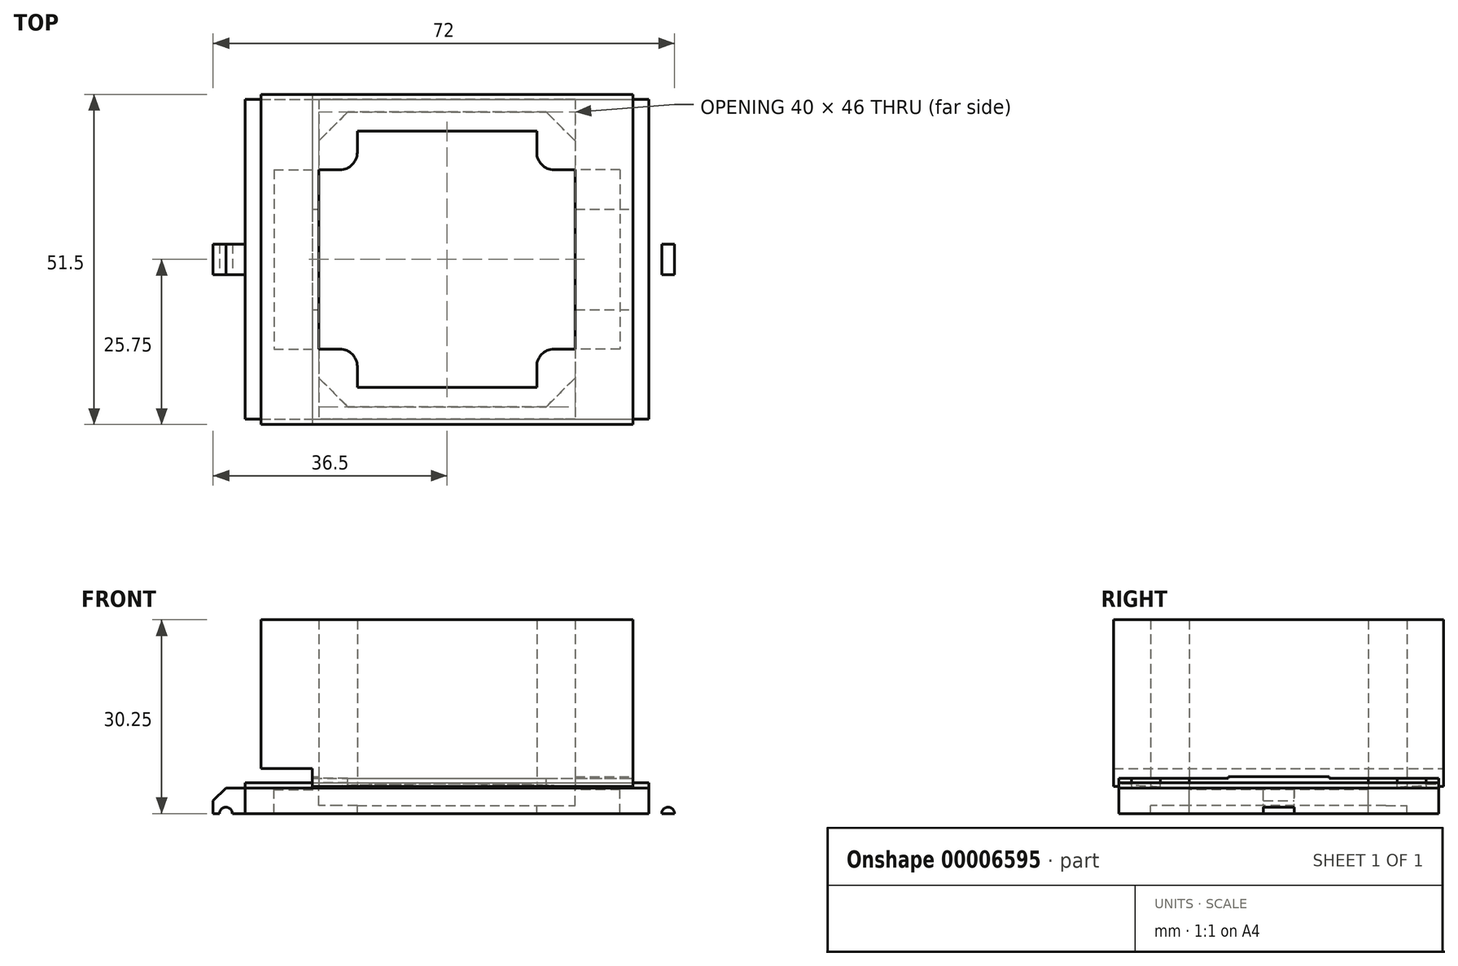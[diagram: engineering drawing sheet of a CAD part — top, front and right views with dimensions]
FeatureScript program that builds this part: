
annotation { "Feature Type Name" : "Feature", "Feature Type Description" : "" }
export const myFeature = defineFeature(function(context is Context, id is Id, definition is map)
    precondition{}
    {
        {
            var Q0;
            Q0=qCreatedBy(makeId("Top.planeOp"),FACE);
            var sketch = newSketch(context, id + "F0", { "sketchPlane" : qUnion([Q0])});
            skLineSegment(sketch, "E0.bottom", {"start": v(0, 0) * mm, "end": v(-58, 0) * mm});
            skLineSegment(sketch, "E0.top", {"start": v(0, 51.5) * mm, "end": v(-58, 51.5) * mm});
            skLineSegment(sketch, "E0.left", {"start": v(0, 0) * mm, "end": v(0, 51.5) * mm});
            skLineSegment(sketch, "E0.right", {"start": v(-58, 0) * mm, "end": v(-58, 51.5) * mm});
            skLineSegment(sketch, "E1", {"start": v(-50, 51.5) * mm, "end": v(-50, 0) * mm});
            skLineSegment(sketch, "E2", {"start": v(-50, 50.7) * mm, "end": v(0, 50.7) * mm});
            skLineSegment(sketch, "E3", {"start": v(-50, 33.6) * mm, "end": v(0, 33.6) * mm});
            skPoint(sketch, "E4", {"position": v(0, 25.75) * mm});
            skLineSegment(sketch, "E5", {"start": v(0, 25.75) * mm, "end": v(-50, 25.75) * mm, "construction": true});
            skLineSegment(sketch, "E6.0.MirrorCS", {"start": v(-50, 0.8) * mm, "end": v(0, 0.8) * mm});
            skLineSegment(sketch, "E6.1.MirrorCS", {"start": v(-50, 17.9) * mm, "end": v(0, 17.9) * mm});
            skSolve(sketch);
        }
        {
            var Q0;
            {var subQ9=sQuery(id+"F0.wireOp",EDGE,"E0.right");Q0=makeQuery(id+"F0.imprint","IMPRINT",FACE,{"disambiguationData":[TD([[makeQuery(id+"F0.imprint","IMPRINT",EDGE,{"derivedFrom":subQ9}),-1.0]])]});}
            var Q1;
            {var subQ1=sQuery(id+"F0.wireOp",EDGE,"E2");Q1=makeQuery(id+"F0.imprint","IMPRINT",FACE,{"disambiguationData":[TD([[makeQuery(id+"F0.imprint","IMPRINT",EDGE,{"derivedFrom":subQ1}),1.0]])]});}
            var Q2;
            {var subQ1=sQuery(id+"F0.wireOp",EDGE,"E2");Q2=makeQuery(id+"F0.imprint","IMPRINT",FACE,{"disambiguationData":[TD([[makeQuery(id+"F0.imprint","IMPRINT",EDGE,{"derivedFrom":subQ1}),-1.0]])]});}
            var Q3;
            {var subQ1=sQuery(id+"F0.wireOp",EDGE,"E3");Q3=makeQuery(id+"F0.imprint","IMPRINT",FACE,{"disambiguationData":[TD([[makeQuery(id+"F0.imprint","IMPRINT",EDGE,{"derivedFrom":subQ1}),-1.0]])]});}
            var Q4;
            {var subQ1=sQuery(id+"F0.wireOp",EDGE,"E6.0.MirrorCS");Q4=makeQuery(id+"F0.imprint","IMPRINT",FACE,{"disambiguationData":[TD([[makeQuery(id+"F0.imprint","IMPRINT",EDGE,{"derivedFrom":subQ1}),1.0]])]});}
            var Q5;
            {var subQ0=sQuery(id+"F0.wireOp",EDGE,"E6.0.MirrorCS");Q5=makeQuery(id+"F0.imprint","IMPRINT",FACE,{"disambiguationData":[TD([[makeQuery(id+"F0.imprint","IMPRINT",EDGE,{"derivedFrom":subQ0}),-1.0]])]});}
            extrude(context, id + "F1", {"entities" : qUnion([Q0, Q1, Q2, Q3, Q4, Q5]), "depth" : 26 * mm});
        }
        {
            var Q0;
            {var subQ1=sQuery(id+"F0.wireOp",EDGE,"E6.0.MirrorCS");Q0=makeQuery(id+"F0.imprint","IMPRINT",FACE,{"disambiguationData":[TD([[makeQuery(id+"F0.imprint","IMPRINT",EDGE,{"derivedFrom":subQ1}),1.0]])]});}
            var Q1;
            {var subQ1=sQuery(id+"F0.wireOp",EDGE,"E2");Q1=makeQuery(id+"F0.imprint","IMPRINT",FACE,{"disambiguationData":[TD([[makeQuery(id+"F0.imprint","IMPRINT",EDGE,{"derivedFrom":subQ1}),-1.0]])]});}
            extrude(context, id + "F2", {"entities" : qUnion([Q0, Q1]), "operationType" : NewBodyOperationType.REMOVE, "depth" : 1.25 * mm});
        }
        {
            var Q0;
            {var subQ1=sQuery(id+"F0.wireOp",EDGE,"E3");Q0=makeQuery(id+"F0.imprint","IMPRINT",FACE,{"disambiguationData":[TD([[makeQuery(id+"F0.imprint","IMPRINT",EDGE,{"derivedFrom":subQ1}),-1.0]])]});}
            extrude(context, id + "F3", {"entities" : qUnion([Q0]), "operationType" : NewBodyOperationType.REMOVE, "depth" : 1.5 * mm});
        }
        {
            var Q0;
            {var subQ9=sQuery(id+"F0.wireOp",EDGE,"E0.right");Q0=makeQuery(id+"F0.imprint","IMPRINT",FACE,{"disambiguationData":[TD([[makeQuery(id+"F0.imprint","IMPRINT",EDGE,{"derivedFrom":subQ9}),-1.0]])]});}
            extrude(context, id + "F4", {"entities" : qUnion([Q0]), "operationType" : NewBodyOperationType.REMOVE, "depth" : 2.75 * mm});
        }
        {
            var Q0;
            Q0=makeQuery(id+"F2.boolean.opBoolean","COPY",FACE,{"derivedFrom":makeQuery(id+"F2.opExtrude","CAP_FACE",FACE,{"disambiguationData":[OSD([sQuery(id+"F0.wireOp",EDGE,"E0.left"),sQuery(id+"F0.wireOp",EDGE,"E1"),sQuery(id+"F0.wireOp",EDGE,"E6.0.MirrorCS"),sQuery(id+"F0.wireOp",EDGE,"E6.1.MirrorCS")])],"isStart":false})});
            var sketch = newSketch(context, id + "F5", { "sketchPlane" : qUnion([Q0])});
            skLineSegment(sketch, "E7.bottom", {"start": v(-49, -45.75) * mm, "end": v(-9, -45.75) * mm});
            skLineSegment(sketch, "E7.top", {"start": v(-49, -5.75) * mm, "end": v(-9, -5.75) * mm});
            skLineSegment(sketch, "E7.left", {"start": v(-49, -45.75) * mm, "end": v(-49, -5.75) * mm});
            skLineSegment(sketch, "E7.right", {"start": v(-9, -45.75) * mm, "end": v(-9, -5.75) * mm});
            skLineSegment(sketch, "E8.bottom", {"start": v(-49, -48.75) * mm, "end": v(-9, -48.75) * mm});
            skLineSegment(sketch, "E8.top", {"start": v(-49, -2.75) * mm, "end": v(-9, -2.75) * mm});
            skLineSegment(sketch, "E8.left", {"start": v(-49, -48.75) * mm, "end": v(-49, -45.75) * mm});
            skLineSegment(sketch, "E8.right", {"start": v(-9, -48.75) * mm, "end": v(-9, -2.75) * mm});
            skLineSegment(sketch, "E9", {"start": v(-49, -5.75) * mm, "end": v(-49, -2.75) * mm});
            skLineSegment(sketch, "E10", {"start": v(-44.5, -48.75) * mm, "end": v(-49, -44.25) * mm});
            skPoint(sketch, "E11", {"position": v(-43, -5.75) * mm});
            skArc(sketch, "E12", {"start": v(-44.5, -48.75) * mm, "mid": v(-45.82, -45.57) * mm, "end": v(-49, -44.25) * mm, "construction": true});
            skArc(sketch, "E13", {"start": v(-49, -11.75) * mm, "mid": v(-44.76, -10) * mm, "end": v(-43, -5.75) * mm, "construction": true});
            skPoint(sketch, "E14", {"position": v(-49, -11.75) * mm});
            skLineSegment(sketch, "E15", {"start": v(-49, -11.75) * mm, "end": v(-45.7, -11.75) * mm});
            skLineSegment(sketch, "E16", {"start": v(-43, -9.05) * mm, "end": v(-43, -5.75) * mm});
            skPoint(sketch, "E17.visualSharp", {"position": v(-43, -11.75) * mm});
            skArc(sketch, "E17.filletArc", {"start": v(-45.7, -11.75) * mm, "mid": v(-43.8, -10.96) * mm, "end": v(-43, -9.05) * mm});
            skLineSegment(sketch, "E18.1.0", {"start": v(-43, -45.75) * mm, "end": v(-43, -42.45) * mm});
            skArc(sketch, "E18.1.1", {"start": v(-43, -42.45) * mm, "mid": v(-43.8, -40.54) * mm, "end": v(-45.7, -39.75) * mm});
            skLineSegment(sketch, "E18.1.2", {"start": v(-45.7, -39.75) * mm, "end": v(-49, -39.75) * mm});
            skLineSegment(sketch, "E18.2.0", {"start": v(-2, -39.75) * mm, "end": v(-12.3, -39.75) * mm});
            skArc(sketch, "E18.2.1", {"start": v(-12.3, -39.75) * mm, "mid": v(-14.2, -40.54) * mm, "end": v(-15, -42.45) * mm});
            skLineSegment(sketch, "E18.2.2", {"start": v(-15, -42.45) * mm, "end": v(-15, -45.75) * mm});
            skLineSegment(sketch, "E18.3.0", {"start": v(-15, -5.75) * mm, "end": v(-15, -9.05) * mm});
            skArc(sketch, "E18.3.1", {"start": v(-15, -9.05) * mm, "mid": v(-14.2, -10.96) * mm, "end": v(-12.3, -11.75) * mm});
            skLineSegment(sketch, "E18.3.2", {"start": v(-12.3, -11.75) * mm, "end": v(-9, -11.75) * mm});
            skPoint(sketch, "E18.center", {"position": v(-29, -25.75) * mm});
            skLineSegment(sketch, "E19", {"start": v(-29, -25.75) * mm, "end": v(-49, -25.75) * mm, "construction": true});
            skLineSegment(sketch, "E20", {"start": v(-29, -25.75) * mm, "end": v(-29, -45.75) * mm, "construction": true});
            skLineSegment(sketch, "E21.0.MirrorCS", {"start": v(-44.5, -2.75) * mm, "end": v(-49, -7.25) * mm});
            skLineSegment(sketch, "E22.0.MirrorCS", {"start": v(-13.5, -48.75) * mm, "end": v(-9, -44.25) * mm});
            skLineSegment(sketch, "E23.0.MirrorCS", {"start": v(-13.5, -2.75) * mm, "end": v(-9, -7.25) * mm});
            skLineSegment(sketch, "E24.0", {"start": v(0, -25.75) * mm, "end": v(-50, -25.75) * mm, "construction": true});
            skLineSegment(sketch, "E25.0", {"start": v(0, 0) * mm, "end": v(-58, 0) * mm});
            skPoint(sketch, "E26", {"position": v(-29, 0) * mm});
            skPoint(sketch, "E27.orphan", {"position": v(-9, -39.75) * mm});
            skLineSegment(sketch, "E28", {"start": v(-2, -39.75) * mm, "end": v(-2, -11.75) * mm});
            skLineSegment(sketch, "E29", {"start": v(-2, -11.75) * mm, "end": v(-9, -11.75) * mm});
            skPoint(sketch, "E30", {"position": v(-6, -39.75) * mm});
            skLineSegment(sketch, "E31", {"start": v(-6, -39.75) * mm, "end": v(-6, -11.75) * mm});
            skLineSegment(sketch, "E32.0.MirrorCS", {"start": v(-56, -39.75) * mm, "end": v(-45.7, -39.75) * mm});
            skLineSegment(sketch, "E32.1.MirrorCS", {"start": v(-56, -39.75) * mm, "end": v(-56, -11.75) * mm});
            skLineSegment(sketch, "E32.2.MirrorCS", {"start": v(-56, -11.75) * mm, "end": v(-49, -11.75) * mm});
            skLineSegment(sketch, "E32.3.MirrorCS", {"start": v(-52, -39.75) * mm, "end": v(-52, -11.75) * mm});
            skSolve(sketch);
        }
        {
            var Q0;
            {var subQ1=sQuery(id+"F5.wireOp",EDGE,"E7.bottom");var subQ9=makeQuery(id+"F5.imprint","INTERSECT",VERTEX,{"derivedFrom":[subQ1,sQuery(id+"F5.wireOp",EDGE,"E18.1.0")]});Q0=makeQuery(id+"F5.imprint","IMPRINT",FACE,{"disambiguationData":[TD([[makeQuery(id+"F5.imprint","IMPRINT",EDGE,{"disambiguationData":[TD([[subQ9,1.0]])],"derivedFrom":subQ1}),-1.0]])]});}
            var Q1;
            {var subQ0=sQuery(id+"F5.wireOp",EDGE,"E18.1.0");Q1=makeQuery(id+"F5.imprint","IMPRINT",FACE,{"disambiguationData":[TD([[makeQuery(id+"F5.imprint","IMPRINT",EDGE,{"derivedFrom":subQ0}),1.0]])]});}
            var Q2;
            {var subQ6=sQuery(id+"F5.wireOp",EDGE,"E18.2.1");Q2=makeQuery(id+"F5.imprint","IMPRINT",FACE,{"disambiguationData":[TD([[makeQuery(id+"F5.imprint","IMPRINT",EDGE,{"derivedFrom":subQ6}),1.0]])]});}
            var Q3;
            {var subQ10=sQuery(id+"F5.wireOp",EDGE,"E18.1.0");Q3=makeQuery(id+"F5.imprint","IMPRINT",FACE,{"disambiguationData":[TD([[makeQuery(id+"F5.imprint","IMPRINT",EDGE,{"derivedFrom":subQ10}),-1.0]])]});}
            var Q4;
            {var subQ7=sQuery(id+"F5.wireOp",EDGE,"E15");Q4=makeQuery(id+"F5.imprint","IMPRINT",FACE,{"disambiguationData":[TD([[makeQuery(id+"F5.imprint","IMPRINT",EDGE,{"derivedFrom":subQ7}),-1.0]])]});}
            var Q5;
            {var subQ6=sQuery(id+"F5.wireOp",EDGE,"E15");Q5=makeQuery(id+"F5.imprint","IMPRINT",FACE,{"disambiguationData":[TD([[makeQuery(id+"F5.imprint","IMPRINT",EDGE,{"derivedFrom":subQ6}),1.0]])]});}
            var Q6;
            {var subQ6=sQuery(id+"F5.wireOp",EDGE,"E18.3.0");Q6=makeQuery(id+"F5.imprint","IMPRINT",FACE,{"disambiguationData":[TD([[makeQuery(id+"F5.imprint","IMPRINT",EDGE,{"derivedFrom":subQ6}),1.0]])]});}
            var Q7;
            {var subQ1=sQuery(id+"F5.wireOp",EDGE,"E7.top");var subQ8=makeQuery(id+"F5.imprint","INTERSECT",VERTEX,{"derivedFrom":[subQ1,sQuery(id+"F5.wireOp",EDGE,"E16")]});Q7=makeQuery(id+"F5.imprint","IMPRINT",FACE,{"disambiguationData":[TD([[makeQuery(id+"F5.imprint","IMPRINT",EDGE,{"disambiguationData":[TD([[subQ8,1.0]])],"derivedFrom":subQ1}),1.0]])]});}
            extrude(context, id + "F6", {"entities" : qUnion([Q0, Q1, Q2, Q3, Q4, Q5, Q6, Q7]), "depth" : 1.5 * mm});
        }
        {
            var Q0;
            {var subQ10=sQuery(id+"F5.wireOp",EDGE,"E18.1.0");Q0=makeQuery(id+"F5.imprint","IMPRINT",FACE,{"disambiguationData":[TD([[makeQuery(id+"F5.imprint","IMPRINT",EDGE,{"derivedFrom":subQ10}),-1.0]])]});}
            var Q1;
            {var subQ7=sQuery(id+"F5.wireOp",EDGE,"E15");Q1=makeQuery(id+"F5.imprint","IMPRINT",FACE,{"disambiguationData":[TD([[makeQuery(id+"F5.imprint","IMPRINT",EDGE,{"derivedFrom":subQ7}),-1.0]])]});}
            extrude(context, id + "F7", {"entities" : qUnion([Q0, Q1]), "operationType" : NewBodyOperationType.ADD, "depth" : 4.25 * mm});
        }
        {
            var Q0;
            {var subQ0=sQuery(id+"F5.wireOp",EDGE,"E8.top");var subQ1=sQuery(id+"F5.wireOp",EDGE,"E8.right");var subQ2=sQuery(id+"F5.wireOp",EDGE,"E7.left");var subQ3=sQuery(id+"F5.wireOp",EDGE,"E21.0.MirrorCS");var subQ4=sQuery(id+"F5.wireOp",EDGE,"E23.0.MirrorCS");Q0=makeQuery(id+"F7.boolean.opBoolean","SPLIT",FACE,{"disambiguationData":[TD([makeQuery(id+"F6.opExtrude","SWEPT_FACE",FACE,{"disambiguationData":[OSD([subQ0])]})])],"derivedFrom":makeQuery(id+"F6.opExtrude","CAP_FACE",FACE,{"disambiguationData":[OSD([sQuery(id+"F5.wireOp",EDGE,"E8.bottom"),subQ0,subQ1,subQ2,sQuery(id+"F5.wireOp",EDGE,"E10"),subQ3,sQuery(id+"F5.wireOp",EDGE,"E22.0.MirrorCS"),subQ4])],"isStart":false})});}
            var sketch = newSketch(context, id + "F8", { "sketchPlane" : qUnion([Q0])});
            skLineSegment(sketch, "E33.0", {"start": v(-2, -11.75) * mm, "end": v(-9, -11.75) * mm});
            skLineSegment(sketch, "E34.0", {"start": v(-6, -39.75) * mm, "end": v(-6, -11.75) * mm});
            skLineSegment(sketch, "E35.0", {"start": v(-2, -39.75) * mm, "end": v(-2, -11.75) * mm});
            skLineSegment(sketch, "E36.0", {"start": v(-2, -39.75) * mm, "end": v(-12.3, -39.75) * mm});
            skLineSegment(sketch, "E37.0", {"start": v(-9, -45.75) * mm, "end": v(-9, -5.75) * mm});
            skLineSegment(sketch, "E38.0.0", {"start": v(-56, -39.75) * mm, "end": v(-56, -11.75) * mm});
            skLineSegment(sketch, "E38.0.1", {"start": v(-56, -39.75) * mm, "end": v(-52, -39.75) * mm});
            skLineSegment(sketch, "E38.0.2", {"start": v(-52, -39.75) * mm, "end": v(-52, -11.75) * mm});
            skLineSegment(sketch, "E38.0.3", {"start": v(-56, -11.75) * mm, "end": v(-52, -11.75) * mm});
            skLineSegment(sketch, "E39.0", {"start": v(-56, -11.75) * mm, "end": v(-49, -11.75) * mm});
            skLineSegment(sketch, "E40.0", {"start": v(-56, -39.75) * mm, "end": v(-45.7, -39.75) * mm});
            skLineSegment(sketch, "E41.0", {"start": v(-49, -45.75) * mm, "end": v(-49, -5.75) * mm});
            skLineSegment(sketch, "E42.bottom", {"start": v(-60.5, -23.35) * mm, "end": v(-65.5, -23.35) * mm});
            skLineSegment(sketch, "E42.top", {"start": v(-60.5, -28.15) * mm, "end": v(-65.5, -28.15) * mm});
            skLineSegment(sketch, "E42.right", {"start": v(-65.5, -23.35) * mm, "end": v(-65.5, -28.15) * mm});
            skLineSegment(sketch, "E43.0", {"start": v(-60.5, -0.8) * mm, "end": v(2.5, -0.8) * mm});
            skLineSegment(sketch, "E44.0", {"start": v(0, -0.8) * mm, "end": v(0, -17.9) * mm});
            skLineSegment(sketch, "E45.0", {"start": v(0, -17.9) * mm, "end": v(0, -33.6) * mm});
            skLineSegment(sketch, "E46.0", {"start": v(0, -33.6) * mm, "end": v(0, -50.7) * mm});
            skLineSegment(sketch, "E47.0", {"start": v(-60.5, -50.7) * mm, "end": v(2.5, -50.7) * mm});
            skLineSegment(sketch, "E48.0", {"start": v(-60.5, 0) * mm, "end": v(-60.5, -50.7) * mm});
            skPoint(sketch, "E49.orphan", {"position": v(-50, -0.8) * mm});
            skPoint(sketch, "E50.orphan", {"position": v(-50, -50.7) * mm});
            skLineSegment(sketch, "E51.0", {"start": v(-44.5, -2.75) * mm, "end": v(-49, -7.25) * mm});
            skLineSegment(sketch, "E52.0", {"start": v(-44.5, -2.75) * mm, "end": v(-13.5, -2.75) * mm});
            skLineSegment(sketch, "E53.0", {"start": v(-13.5, -2.75) * mm, "end": v(-9, -7.25) * mm});
            skLineSegment(sketch, "E54.0", {"start": v(-13.5, -48.75) * mm, "end": v(-9, -44.25) * mm});
            skLineSegment(sketch, "E55.0", {"start": v(-44.5, -48.75) * mm, "end": v(-13.5, -48.75) * mm});
            skLineSegment(sketch, "E56.0", {"start": v(-44.5, -48.75) * mm, "end": v(-49, -44.25) * mm});
            skLineSegment(sketch, "E57.0", {"start": v(-49, -11.75) * mm, "end": v(-45.7, -11.75) * mm});
            skArc(sketch, "E58.0", {"start": v(-45.7, -11.75) * mm, "mid": v(-43.8, -10.96) * mm, "end": v(-43, -9.05) * mm});
            skLineSegment(sketch, "E59.0", {"start": v(-43, -9.05) * mm, "end": v(-43, -5.75) * mm});
            skLineSegment(sketch, "E60.0", {"start": v(-43, -5.75) * mm, "end": v(-15, -5.75) * mm});
            skArc(sketch, "E61.0", {"start": v(-15, -9.05) * mm, "mid": v(-14.2, -10.96) * mm, "end": v(-12.3, -11.75) * mm});
            skLineSegment(sketch, "E62.0", {"start": v(-12.3, -11.75) * mm, "end": v(-9, -11.75) * mm});
            skLineSegment(sketch, "E63.0", {"start": v(-15, -5.75) * mm, "end": v(-15, -9.05) * mm});
            skLineSegment(sketch, "E64.0", {"start": v(-9, -39.75) * mm, "end": v(-12.3, -39.75) * mm});
            skArc(sketch, "E65.0", {"start": v(-12.3, -39.75) * mm, "mid": v(-14.2, -40.54) * mm, "end": v(-15, -42.45) * mm});
            skLineSegment(sketch, "E66.0", {"start": v(-15, -42.45) * mm, "end": v(-15, -45.75) * mm});
            skLineSegment(sketch, "E67.0", {"start": v(-43, -45.75) * mm, "end": v(-15, -45.75) * mm});
            skLineSegment(sketch, "E68.0", {"start": v(-43, -45.75) * mm, "end": v(-43, -42.45) * mm});
            skArc(sketch, "E69.0", {"start": v(-43, -42.45) * mm, "mid": v(-43.8, -40.54) * mm, "end": v(-45.7, -39.75) * mm});
            skLineSegment(sketch, "E70.0", {"start": v(-49, -39.75) * mm, "end": v(-45.7, -39.75) * mm});
            skLineSegment(sketch, "E71.0", {"start": v(-29, -25.75) * mm, "end": v(-29, -45.75) * mm, "construction": true});
            skLineSegment(sketch, "E72.0", {"start": v(0, -25.75) * mm, "end": v(-50, -25.75) * mm, "construction": true});
            skPoint(sketch, "E73", {"position": v(-65.5, -25.75) * mm});
            skLineSegment(sketch, "E74.0.MirrorCS", {"start": v(2.5, -23.35) * mm, "end": v(7.5, -23.35) * mm});
            skLineSegment(sketch, "E75.0.MirrorCS", {"start": v(7.5, -23.35) * mm, "end": v(7.5, -28.15) * mm});
            skLineSegment(sketch, "E76.0.MirrorCS", {"start": v(2.5, -28.15) * mm, "end": v(7.5, -28.15) * mm});
            skPoint(sketch, "E77.0", {"position": v(-58, 0) * mm});
            skLineSegment(sketch, "E78.0.MirrorCS", {"start": v(2.5, 0) * mm, "end": v(2.5, -50.7) * mm});
            skPoint(sketch, "E79.orphan", {"position": v(0, -0.8) * mm});
            skPoint(sketch, "E80.orphan", {"position": v(0, -50.7) * mm});
            skSolve(sketch);
        }
        {
            var Q0;
            {var subQ2=sQuery(id+"F8.wireOp",EDGE,"E38.0.0");Q0=makeQuery(id+"F8.imprint","IMPRINT",FACE,{"disambiguationData":[TD([[makeQuery(id+"F8.imprint","IMPRINT",EDGE,{"derivedFrom":subQ2}),-1.0]])]});}
            var Q1;
            {var subQ5=sQuery(id+"F8.wireOp",EDGE,"E38.0.2");Q1=makeQuery(id+"F8.imprint","IMPRINT",FACE,{"disambiguationData":[TD([[makeQuery(id+"F8.imprint","IMPRINT",EDGE,{"derivedFrom":subQ5}),-1.0]])]});}
            var Q2;
            {var subQ5=sQuery(id+"F8.wireOp",EDGE,"E34.0");Q2=makeQuery(id+"F8.imprint","IMPRINT",FACE,{"disambiguationData":[TD([[makeQuery(id+"F8.imprint","IMPRINT",EDGE,{"derivedFrom":subQ5}),1.0]])]});}
            var Q3;
            {var subQ2=sQuery(id+"F8.wireOp",EDGE,"E34.0");Q3=makeQuery(id+"F8.imprint","IMPRINT",FACE,{"disambiguationData":[TD([[makeQuery(id+"F8.imprint","IMPRINT",EDGE,{"derivedFrom":subQ2}),-1.0]])]});}
            extrude(context, id + "F9", {"entities" : qUnion([Q0, Q1, Q2, Q3]), "operationType" : NewBodyOperationType.ADD, "depth" : 0.3 * mm});
        }
        {
            var Q0;
            {var subQ13=sQuery(id+"F8.wireOp",EDGE,"E35.0");Q0=makeQuery(id+"F8.imprint","IMPRINT",FACE,{"disambiguationData":[TD([[makeQuery(id+"F8.imprint","IMPRINT",EDGE,{"derivedFrom":subQ13}),-1.0]])]});}
            var Q1;
            {var subQ2=sQuery(id+"F8.wireOp",EDGE,"E42.bottom");Q1=makeQuery(id+"F8.imprint","IMPRINT",FACE,{"disambiguationData":[TD([[makeQuery(id+"F8.imprint","IMPRINT",EDGE,{"derivedFrom":subQ2}),1.0]])]});}
            var Q2;
            {var subQ3=sQuery(id+"F8.wireOp",EDGE,"E51.0");Q2=makeQuery(id+"F8.imprint","IMPRINT",FACE,{"disambiguationData":[TD([[makeQuery(id+"F8.imprint","IMPRINT",EDGE,{"derivedFrom":subQ3}),1.0]])]});}
            var Q3;
            {var subQ3=sQuery(id+"F8.wireOp",EDGE,"E54.0");Q3=makeQuery(id+"F8.imprint","IMPRINT",FACE,{"disambiguationData":[TD([[makeQuery(id+"F8.imprint","IMPRINT",EDGE,{"derivedFrom":subQ3}),1.0]])]});}
            var Q4;
            {var subQ1=sQuery(id+"F8.wireOp",EDGE,"E74.0.MirrorCS");Q4=makeQuery(id+"F8.imprint","IMPRINT",FACE,{"disambiguationData":[TD([[makeQuery(id+"F8.imprint","IMPRINT",EDGE,{"derivedFrom":subQ1}),-1.0]])]});}
            var Q5;
            {var subQ8=sQuery(id+"F8.wireOp",EDGE,"E44.0");Q5=makeQuery(id+"F8.imprint","IMPRINT",FACE,{"disambiguationData":[TD([[makeQuery(id+"F8.imprint","IMPRINT",EDGE,{"derivedFrom":subQ8}),1.0]])]});}
            extrude(context, id + "F10", {"entities" : qUnion([Q0, Q1, Q2, Q3, Q4, Q5]), "depth" : 4 * mm});
        }
        {
            var Q0;
            Q0=makeQuery(id+"F10.opExtrude","CAP_EDGE",EDGE,{"disambiguationData":[OSD([sQuery(id+"F8.wireOp",EDGE,"E42.right")])],"isStart":true});
            var Q1;
            Q1=makeQuery(id+"F10.opExtrude","CAP_EDGE",EDGE,{"disambiguationData":[OSD([sQuery(id+"F8.wireOp",EDGE,"E75.0.MirrorCS")])],"isStart":true});
            chamfer(context, id + "F11", {"entities" : qUnion([Q0, Q1]), "width" : 2 * mm, "tangentPropagation" : true});
        }
        {
            var Q0;
            Q0=makeQuery(id+"F10.opExtrude","SWEPT_FACE",FACE,{"disambiguationData":[OSD([sQuery(id+"F8.wireOp",EDGE,"E42.bottom")])]});
            var sketch = newSketch(context, id + "F12", { "sketchPlane" : qUnion([Q0])});
            skLineSegment(sketch, "E81.0.0", {"start": v(-60.5, -0.25) * mm, "end": v(-63.5, -0.25) * mm});
            skLineSegment(sketch, "E81.0.1", {"start": v(-63.5, -0.25) * mm, "end": v(-65.5, -2.25) * mm});
            skLineSegment(sketch, "E81.0.2", {"start": v(-65.5, -2.25) * mm, "end": v(-65.5, -4.25) * mm});
            skLineSegment(sketch, "E81.0.3", {"start": v(-65.5, -4.25) * mm, "end": v(-60.5, -4.25) * mm});
            skLineSegment(sketch, "E81.0.4", {"start": v(-60.5, -4.25) * mm, "end": v(-60.5, -0.25) * mm});
            skLineSegment(sketch, "E82.0.0", {"start": v(2.5, -0.25) * mm, "end": v(-60.5, -0.25) * mm});
            skLineSegment(sketch, "E82.0.1", {"start": v(-60.5, -0.25) * mm, "end": v(-60.5, -4.25) * mm});
            skLineSegment(sketch, "E82.0.2", {"start": v(-60.5, -4.25) * mm, "end": v(2.5, -4.25) * mm});
            skLineSegment(sketch, "E82.0.3", {"start": v(2.5, -4.25) * mm, "end": v(2.5, -0.25) * mm});
            skLineSegment(sketch, "E83.0.0", {"start": v(7.5, -4.25) * mm, "end": v(7.5, -2.25) * mm});
            skLineSegment(sketch, "E83.0.1", {"start": v(7.5, -2.25) * mm, "end": v(5.5, -0.25) * mm});
            skLineSegment(sketch, "E83.0.2", {"start": v(5.5, -0.25) * mm, "end": v(2.5, -0.25) * mm});
            skLineSegment(sketch, "E83.0.3", {"start": v(2.5, -0.25) * mm, "end": v(2.5, -4.25) * mm});
            skLineSegment(sketch, "E83.0.4", {"start": v(2.5, -4.25) * mm, "end": v(7.5, -4.25) * mm});
            skLineSegment(sketch, "E84", {"start": v(-63.5, -0.25) * mm, "end": v(-63.5, -4.25) * mm, "construction": true});
            skPoint(sketch, "E85", {"position": v(-29, -4.25) * mm});
            skPoint(sketch, "E86", {"position": v(-29, -0.25) * mm});
            skLineSegment(sketch, "E87", {"start": v(-29, -0.25) * mm, "end": v(-29, -4.25) * mm, "construction": true});
            skArc(sketch, "E88", {"start": v(-62.5, -4.25) * mm, "mid": v(-63.5, -3.25) * mm, "end": v(-64.5, -4.25) * mm});
            skPoint(sketch, "E89", {"position": v(-63.5, -3.25) * mm});
            skArc(sketch, "E90.0.MirrorCS", {"start": v(4.5, -4.25) * mm, "mid": v(5.5, -3.25) * mm, "end": v(6.5, -4.25) * mm});
            skSolve(sketch);
        }
        {
            var Q0;
            {var subQ0=sQuery(id+"F12.wireOp",EDGE,"E88");Q0=makeQuery(id+"F12.imprint","IMPRINT",FACE,{"disambiguationData":[TD([[makeQuery(id+"F12.imprint","IMPRINT",EDGE,{"derivedFrom":subQ0}),1.0]])]});}
            var Q1;
            {var subQ0=sQuery(id+"F12.wireOp",EDGE,"E90.0.MirrorCS");Q1=makeQuery(id+"F12.imprint","IMPRINT",FACE,{"disambiguationData":[TD([[makeQuery(id+"F12.imprint","IMPRINT",EDGE,{"derivedFrom":subQ0}),-1.0]])]});}
            extrude(context, id + "F13", {"entities" : qUnion([Q0, Q1]), "operationType" : NewBodyOperationType.REMOVE, "endBound" : BoundingType.THROUGH_ALL, "oppositeDirection" : true, "depth" : 25 * mm});
        }
        {
            var Q0;
            Q0=makeQuery(id+"F10.opExtrude","SWEPT_FACE",FACE,{"disambiguationData":[OSD([sQuery(id+"F8.wireOp",EDGE,"E43.0")])]});
            var sketch = newSketch(context, id + "F14", { "sketchPlane" : qUnion([Q0])});
            skLineSegment(sketch, "E91.0", {"start": v(-45.7, -0.25) * mm, "end": v(-49, -0.25) * mm});
            skLineSegment(sketch, "E92.0", {"start": v(-43, -0.25) * mm, "end": v(-45.7, -0.25) * mm});
            skLineSegment(sketch, "E93.0", {"start": v(-15, -0.25) * mm, "end": v(-43, -0.25) * mm});
            skLineSegment(sketch, "E94.0", {"start": v(-12.3, -0.25) * mm, "end": v(-15, -0.25) * mm});
            skLineSegment(sketch, "E95.0", {"start": v(-9, -0.25) * mm, "end": v(-12.3, -0.25) * mm});
            skPoint(sketch, "E96", {"position": v(-29, -0.25) * mm});
            skLineSegment(sketch, "E97", {"start": v(-29, -0.25) * mm, "end": v(-29, 0.35) * mm});
            skEllipticalArc(sketch, "E98", {});
            const initialGuessF14  = {"E98": [-0.029, -0.00025, -1, 0, 0.02, 0.0006, 3.141592653589793, 0]};
            skSetInitialGuess(sketch, initialGuessF14);
            skSolve(sketch);
        }
        {
            var Q0;
            {var subQ2=sQuery(id+"F14.wireOp",EDGE,"E91.0");Q0=makeQuery(id+"F14.imprint","IMPRINT",FACE,{"disambiguationData":[TD([[makeQuery(id+"F14.imprint","IMPRINT",EDGE,{"derivedFrom":subQ2}),1.0]])]});}
            var Q1;
            {var subQ3=sQuery(id+"F14.wireOp",EDGE,"E94.0");Q1=makeQuery(id+"F14.imprint","IMPRINT",FACE,{"disambiguationData":[TD([[makeQuery(id+"F14.imprint","IMPRINT",EDGE,{"derivedFrom":subQ3}),1.0]])]});}
            var Q2;
            Q2=makeQuery(id+"F10.opExtrude","SWEPT_FACE",FACE,{"disambiguationData":[OSD([sQuery(id+"F8.wireOp",EDGE,"E47.0")])]});
            extrude(context, id + "F15", {"entities" : qUnion([Q0, Q1]), "operationType" : NewBodyOperationType.ADD, "endBound" : BoundingType.UP_TO_SURFACE, "oppositeDirection" : true, "endBoundEntityFace" : qUnion([Q2]), "depth" : 25 * mm});
        }
        {
            var Q0;
            {var subQ10=sQuery(id+"F8.wireOp",EDGE,"E35.0");Q0=makeQuery(id+"F8.imprint","IMPRINT",FACE,{"disambiguationData":[TD([[makeQuery(id+"F8.imprint","IMPRINT",EDGE,{"derivedFrom":subQ10}),-1.0]])]});}
            var Q1;
            {var subQ2=sQuery(id+"F8.wireOp",EDGE,"E38.0.0");Q1=makeQuery(id+"F8.imprint","IMPRINT",FACE,{"disambiguationData":[TD([[makeQuery(id+"F8.imprint","IMPRINT",EDGE,{"derivedFrom":subQ2}),-1.0]])]});}
            var Q2;
            {var subQ5=sQuery(id+"F8.wireOp",EDGE,"E38.0.2");Q2=makeQuery(id+"F8.imprint","IMPRINT",FACE,{"disambiguationData":[TD([[makeQuery(id+"F8.imprint","IMPRINT",EDGE,{"derivedFrom":subQ5}),-1.0]])]});}
            var Q3;
            {var subQ5=sQuery(id+"F8.wireOp",EDGE,"E34.0");Q3=makeQuery(id+"F8.imprint","IMPRINT",FACE,{"disambiguationData":[TD([[makeQuery(id+"F8.imprint","IMPRINT",EDGE,{"derivedFrom":subQ5}),1.0]])]});}
            var Q4;
            {var subQ2=sQuery(id+"F8.wireOp",EDGE,"E34.0");Q4=makeQuery(id+"F8.imprint","IMPRINT",FACE,{"disambiguationData":[TD([[makeQuery(id+"F8.imprint","IMPRINT",EDGE,{"derivedFrom":subQ2}),-1.0]])]});}
            var Q5;
            {var subQ8=sQuery(id+"F8.wireOp",EDGE,"E44.0");Q5=makeQuery(id+"F8.imprint","IMPRINT",FACE,{"disambiguationData":[TD([[makeQuery(id+"F8.imprint","IMPRINT",EDGE,{"derivedFrom":subQ8}),1.0]])]});}
            var Q6;
            Q6=makeQuery(id+"F6.opExtrude","CAP_FACE",FACE,{"disambiguationData":[OSD([sQuery(id+"F5.wireOp",EDGE,"E8.bottom"),sQuery(id+"F5.wireOp",EDGE,"E8.top"),sQuery(id+"F5.wireOp",EDGE,"E8.right"),sQuery(id+"F5.wireOp",EDGE,"E7.left"),sQuery(id+"F5.wireOp",EDGE,"E10"),sQuery(id+"F5.wireOp",EDGE,"E21.0.MirrorCS"),sQuery(id+"F5.wireOp",EDGE,"E22.0.MirrorCS"),sQuery(id+"F5.wireOp",EDGE,"E23.0.MirrorCS")])],"isStart":true});
            extrude(context, id + "F16", {"entities" : qUnion([Q0, Q1, Q2, Q3, Q4, Q5]), "oppositeDirection" : true, "endBoundEntity" : qUnion([Q6]), "depth" : .8 * mm});
        }
        {
            var Q0;
            {var subQ3=sQuery(id+"F8.wireOp",EDGE,"E57.0");Q0=makeQuery(id+"F8.imprint","IMPRINT",FACE,{"disambiguationData":[TD([[makeQuery(id+"F8.imprint","IMPRINT",EDGE,{"derivedFrom":subQ3}),1.0]])]});}
            extrude(context, id + "F17", {"entities" : qUnion([Q0]), "operationType" : NewBodyOperationType.REMOVE, "endBound" : BoundingType.THROUGH_ALL, "oppositeDirection" : true, "depth" : 25 * mm});
        }
    });
